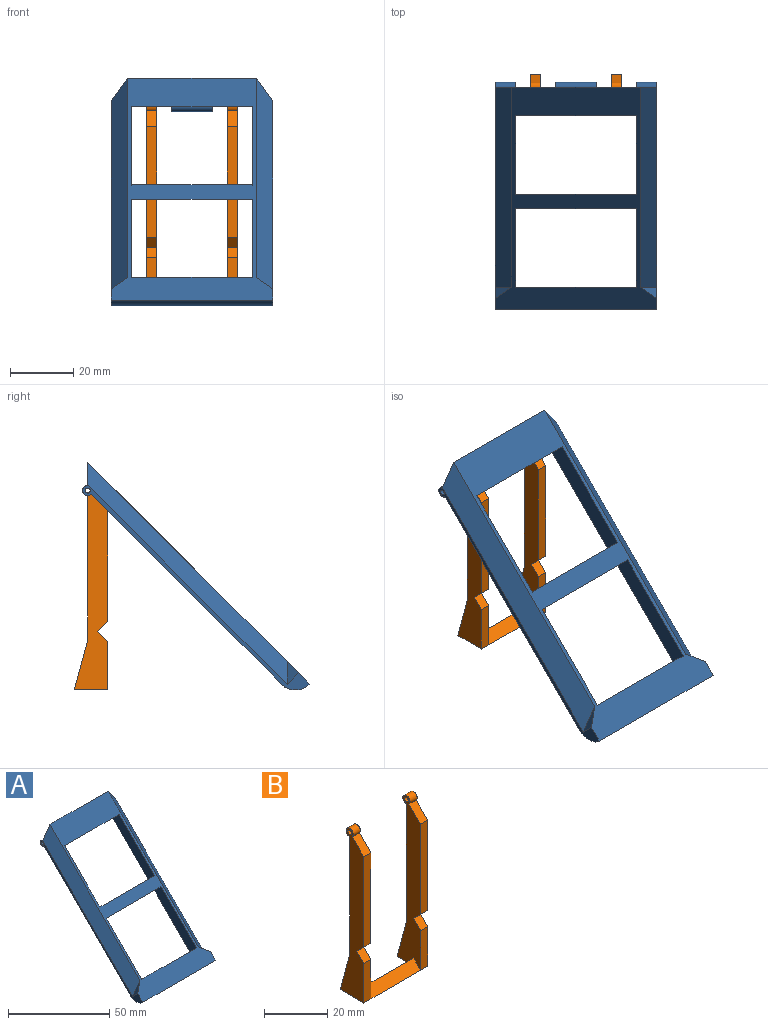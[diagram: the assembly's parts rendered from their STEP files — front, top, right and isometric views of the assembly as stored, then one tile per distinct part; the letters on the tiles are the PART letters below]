
ASSEMBLY  parts=2 mates=1
PART A: 27 faces, bbox 50.8x71.6x71.8 mm
  f0: plane 71.57x64.66mm, normal (1,0,0), area 138.1mm2, adj f2,f4,f6,f9,f11,f17,f18,f26
  f1: plane 71.57x64.66mm, normal (-1,0,0), area 138.1mm2, adj f2,f3,f5,f6,f11,f16,f19,f25
  f2: cylinder r=6.35mm len=50.8mm, axis (-1,0,0), area 420mm2, adj f0,f1,f9,f10,f11,f14,f15,f16
  f3: plane 7.18x5.08mm, normal (-0.71,0.5,0.5), area 18.2mm2, adj f1,f11,f25
  f4: plane 7.18x5.08mm, normal (0.71,0.5,0.5), area 18.2mm2, adj f0,f11,f26
  f5: cylinder r=0.79mm len=6.35mm, axis (-1,0,0), area 31.7mm2, adj f1,f15
  f6: plane 50.8x7.39mm, normal (0,1,0), area 318.9mm2, adj f0,f1,f10,f11,f15,f18,f19,f20
  f7: cylinder r=0.79mm len=12.7mm, axis (-1,0,0), area 63.3mm2, adj f21,f22
  f8: plane 38.1x7.39mm, normal (0,0,-1), area 261.5mm2, adj f10,f11,f15,f20,f21,f22,f23,f24
  f9: plane 59.88x59.88mm, normal (0,0.71,-0.71), area 537.7mm2, adj f0,f2,f10,f18
  f10: plane 64.67x64.45mm, normal (-1,0,0), area 521.2mm2, adj f2,f6,f8,f9,f11,f12,f13,f14
  f11: plane 69.98x69.98mm, normal (0,-0.71,0.71), area 1437.3mm2, adj f0,f1,f2,f3,f4,f6,f8,f10
  f12: plane 38.1x4.49mm, normal (0,0,-1), area 171.1mm2, adj f10,f11,f13,f15
  f13: plane 38.1x4.49mm, normal (0,1,0), area 171.1mm2, adj f10,f11,f12,f15
  f14: plane 38.1x8.41mm, normal (0,1,0), area 320.4mm2, adj f2,f10,f11,f15
  f15: plane 64.67x64.45mm, normal (1,0,0), area 521.2mm2, adj f2,f5,f6,f8,f11,f12,f13,f14
  f16: plane 59.88x59.88mm, normal (0,0.71,-0.71), area 537.7mm2, adj f1,f2,f15,f19
  f17: cylinder r=0.79mm len=6.35mm, axis (-1,0,0), area 31.7mm2, adj f0,f10
  f18: cylinder r=1.59mm len=6.35mm, axis (-1,0,0), area 39.6mm2, adj f0,f6,f9,f10
  f19: cylinder r=1.59mm len=6.35mm, axis (1,0,0), area 39.6mm2, adj f1,f6,f15,f16
  f20: cylinder r=1.59mm len=12.7mm, axis (-1,0,0), area 95mm2, adj f6,f8,f21,f22
  f21: plane 3.97x3.97mm, normal (1,0,0), area 8.4mm2, adj f6,f7,f8,f20,f23
  f22: plane 3.97x3.97mm, normal (-1,0,0), area 8.4mm2, adj f6,f7,f8,f20,f24
  f23: cylinder r=2.38mm len=12.7mm, axis (-1,0,0), area 47.5mm2, adj f6,f8,f10,f21
  f24: cylinder r=2.38mm len=12.7mm, axis (1,0,0), area 47.5mm2, adj f6,f8,f15,f22
  f25: plane 70.05x62.86mm, normal (-0.71,-0.5,0.5), area 638.7mm2, adj f1,f3,f6,f11
  f26: plane 70.05x62.86mm, normal (0.71,-0.5,0.5), area 638.7mm2, adj f0,f4,f6,f11
PART B: 25 faces, bbox 28.6x10.6x64.5 mm
  f0: plane 64.45x10.56mm, normal (-1,0,0), area 396.9mm2, adj f1,f2,f3,f4,f5,f6,f7,f8
  f1: plane 15.24x3.18mm, normal (0,-1,0), area 48.4mm2, adj f0,f2,f9,f11
  f2: plane 28.58x10.56mm, normal (0,0,-1), area 208.2mm2, adj f0,f1,f3,f11,f12,f13,f16,f17
  f3: plane 15.72x4.21mm, normal (0,0.97,0.26), area 51.7mm2, adj f0,f2,f4,f11
  f4: plane 45.56x3.18mm, normal (0,1,0), area 144.6mm2, adj f0,f3,f5,f11
  f5: cylinder r=1.59mm len=3.18mm, axis (-1,0,0), area 27.7mm2, adj f0,f4,f6,f11
  f6: plane 5.23x5.23mm, normal (0,-0.71,0.71), area 23.5mm2, adj f0,f5,f7,f11
  f7: plane 34.93x3.18mm, normal (0,-1,0), area 110.9mm2, adj f0,f6,f8,f11
  f8: plane 3.18x3.18mm, normal (0,-0.71,-0.71), area 14.3mm2, adj f0,f7,f9,f11
  f9: plane 3.18x3.18mm, normal (0,-0.71,0.71), area 14.3mm2, adj f0,f1,f8,f11
  f10: cylinder r=0.79mm len=3.18mm, axis (-1,0,0), area 15.8mm2, adj f0,f11
  f11: plane 64.45x10.56mm, normal (1,0,0), area 407mm2, adj f1,f2,f3,f4,f5,f6,f7,f8
  f12: plane 22.23x3.18mm, normal (0,-0.71,0.71), area 99.8mm2, adj f0,f2,f13,f24
  f13: plane 22.23x3.18mm, normal (0,0.71,0.71), area 99.8mm2, adj f0,f2,f12,f24
  f14: plane 3.18x3.18mm, normal (0,-0.71,-0.71), area 14.3mm2, adj f15,f21,f23,f24
  f15: plane 3.18x3.18mm, normal (0,-0.71,0.71), area 14.3mm2, adj f14,f16,f23,f24
  f16: plane 15.24x3.18mm, normal (0,-1,0), area 48.4mm2, adj f2,f15,f23,f24
  f17: plane 15.72x4.21mm, normal (0,0.97,0.26), area 51.7mm2, adj f2,f18,f23,f24
  f18: plane 45.56x3.18mm, normal (0,1,0), area 144.6mm2, adj f17,f19,f23,f24
  f19: cylinder r=1.59mm len=3.18mm, axis (1,0,0), area 27.7mm2, adj f18,f20,f23,f24
  f20: plane 5.23x5.23mm, normal (0,-0.71,0.71), area 23.5mm2, adj f19,f21,f23,f24
  f21: plane 34.93x3.18mm, normal (0,-1,0), area 110.9mm2, adj f14,f20,f23,f24
  f22: cylinder r=0.79mm len=3.18mm, axis (1,0,0), area 15.8mm2, adj f23,f24
  f23: plane 64.45x10.56mm, normal (-1,0,0), area 407mm2, adj f2,f14,f15,f16,f17,f18,f19,f20
  f24: plane 64.45x10.56mm, normal (1,0,0), area 396.9mm2, adj f2,f12,f13,f14,f15,f16,f17,f18
PLACE A t=(-11.11,9.27,2.63)mm
PLACE B t=(0,-6.35,2.63)mm
MATE revolute A.f5 <-> B.f5  axis (-1,0,0) through (1.59,42.94,35.33)mm
